AUTODESK INVENTOR PART (.ipt)
format: ipt  version: 2019 (Build 230136000, 136)  size: 145,408 bytes
history: native  units: mm (DEFAULTED — no unit token found)
features: plane x5, other x4, split x4, sketch x3
ambient origin geometry x8: Origin, YZ Plane, XZ Plane, XY Plane, X Axis, Y Axis, Z Axis, Center Point
bodies: Solid1 (feature_tree), Body (feature_tree)
feature tree (16):
  parser-record x1  (decoder bookkeeping rows leaked as tree rows — omitted from the tree; the rows remain in map.json)
  other  "Driven Length"
  other  "Start plane"
  other  "End plane"
  plane  "Work Plane4"
  split  "Split1"
  plane  "Work Plane5"
  split  "Split2"
  plane  "Work Plane6"
  split  "Split3"
  plane  "Work Plane7"
  split  "Split4"
  sketch  "Sketch"  dims[d7=4.0mm d9=20.0mm d11=20.0mm d12=2.0mm d13=-0.0mm d14=800.0mm d15=10.0mm d16=10.0mm d17=90.0deg d18=800.0mm]
  sketch  "Sketch3"  dims[d3=800.0mm]
  plane  "Work Plane3"
  sketch  "Sketch4"  dims[d4=0.0mm]
